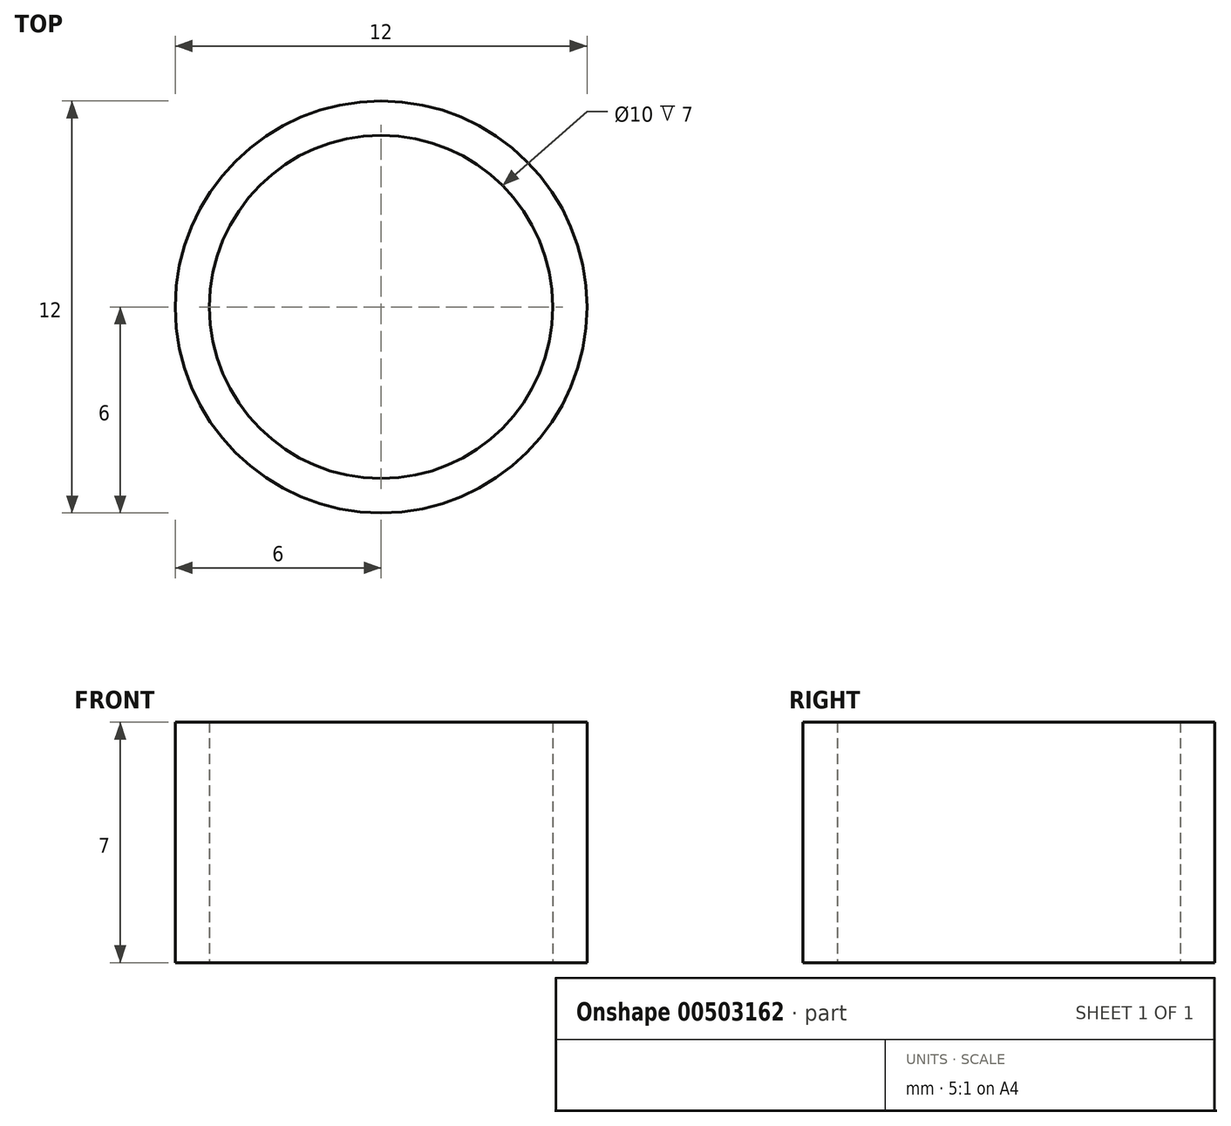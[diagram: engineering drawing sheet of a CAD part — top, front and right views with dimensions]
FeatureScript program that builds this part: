
annotation { "Feature Type Name" : "Feature", "Feature Type Description" : "" }
export const myFeature = defineFeature(function(context is Context, id is Id, definition is map)
    precondition{}
    {
        {
            var Q0;
            Q0=qCreatedBy(makeId("Top.planeOp"),FACE);
            var sketch = newSketch(context, id + "F0", { "sketchPlane" : qUnion([Q0])});
            skCircle(sketch, "E0", {"center": v(0, 0) * mm, "radius": 6 * mm});
            skCircle(sketch, "E1", {"center": v(0, 0) * mm, "radius": 5 * mm});
            skSolve(sketch);
        }
        {
            var Q0;
            Q0=makeQuery(id+"F0.imprint","IMPRINT",FACE,{"disambiguationData":[TD([[makeQuery(id+"F0.imprint","IMPRINT",EDGE,{"derivedFrom":sQuery(id+"F0.wireOp",EDGE,"E0")}),1.0]])]});
            extrude(context, id + "F1", {"entities" : qUnion([Q0]), "depth" : 7 * mm});
        }
    });
